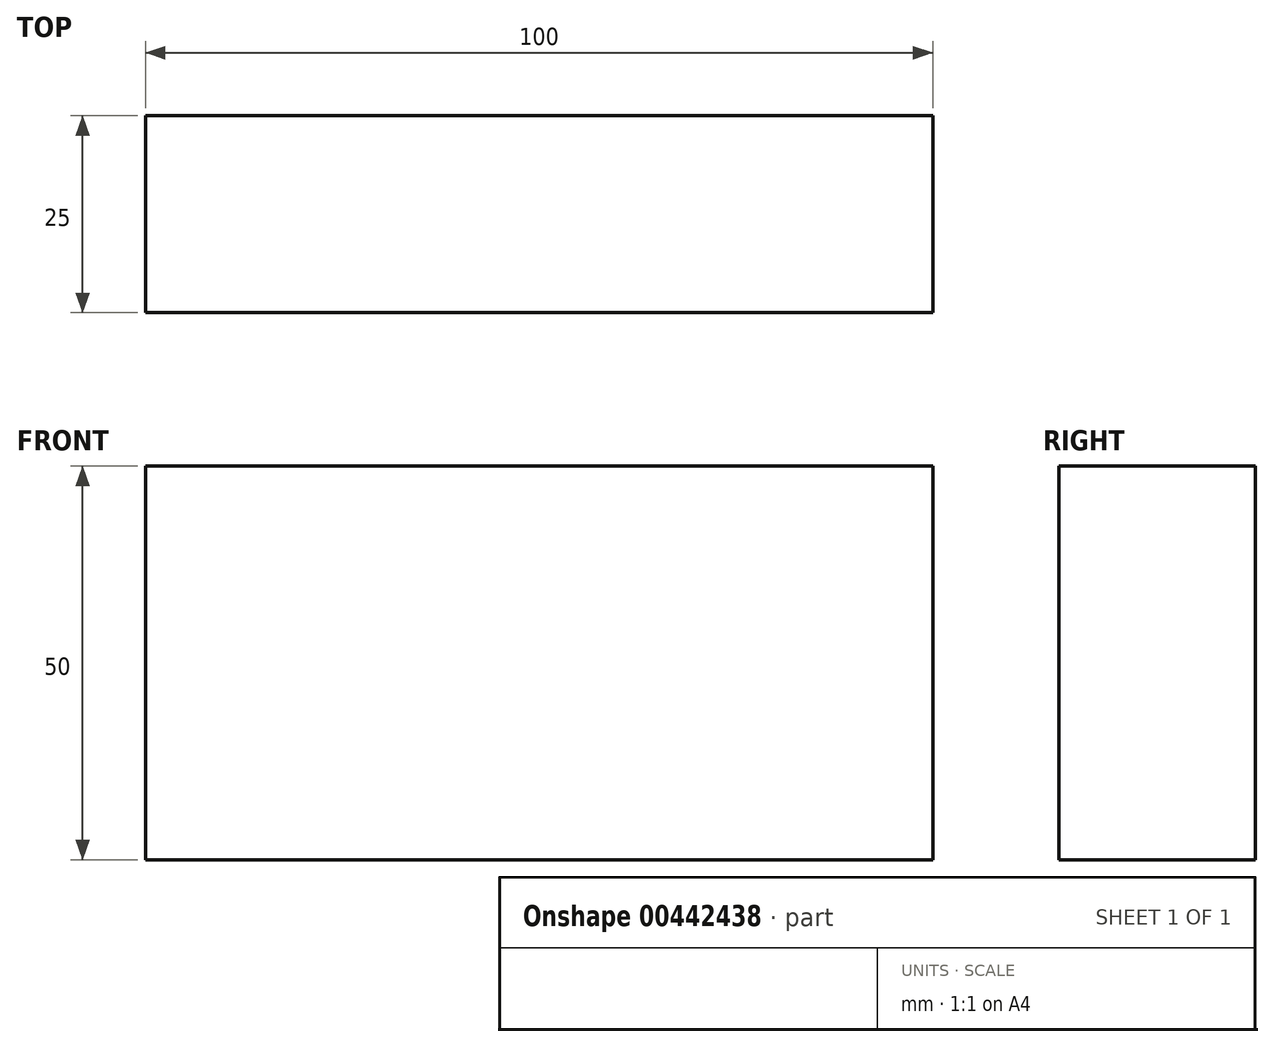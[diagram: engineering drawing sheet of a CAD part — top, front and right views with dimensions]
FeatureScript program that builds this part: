
annotation { "Feature Type Name" : "Feature", "Feature Type Description" : "" }
export const myFeature = defineFeature(function(context is Context, id is Id, definition is map)
    precondition{}
    {
        {
            var Q0;
            Q0=qCreatedBy(makeId("Front.planeOp"),FACE);
            var sketch = newSketch(context, id + "F0", { "sketchPlane" : qUnion([Q0])});
            skLineSegment(sketch, "E0", {"start": v(0, 0) * mm, "end": v(0, -50) * mm});
            skLineSegment(sketch, "E1", {"start": v(0, 0) * mm, "end": v(100, 0) * mm});
            skLineSegment(sketch, "E2", {"start": v(100, 0) * mm, "end": v(100, -50) * mm});
            skLineSegment(sketch, "E3", {"start": v(100, -50) * mm, "end": v(0, -50) * mm});
            skSolve(sketch);
        }
        {
            var Q0;
            Q0=makeQuery(id+"F0.imprint","IMPRINT",FACE,{"disambiguationData":[TD([[makeQuery(id+"F0.imprint","IMPRINT",EDGE,{"derivedFrom":sQuery(id+"F0.wireOp",EDGE,"E0")}),1.0]])]});
            extrude(context, id + "F1", {"entities" : qUnion([Q0]), "depth" : 25 * mm});
        }
    });
